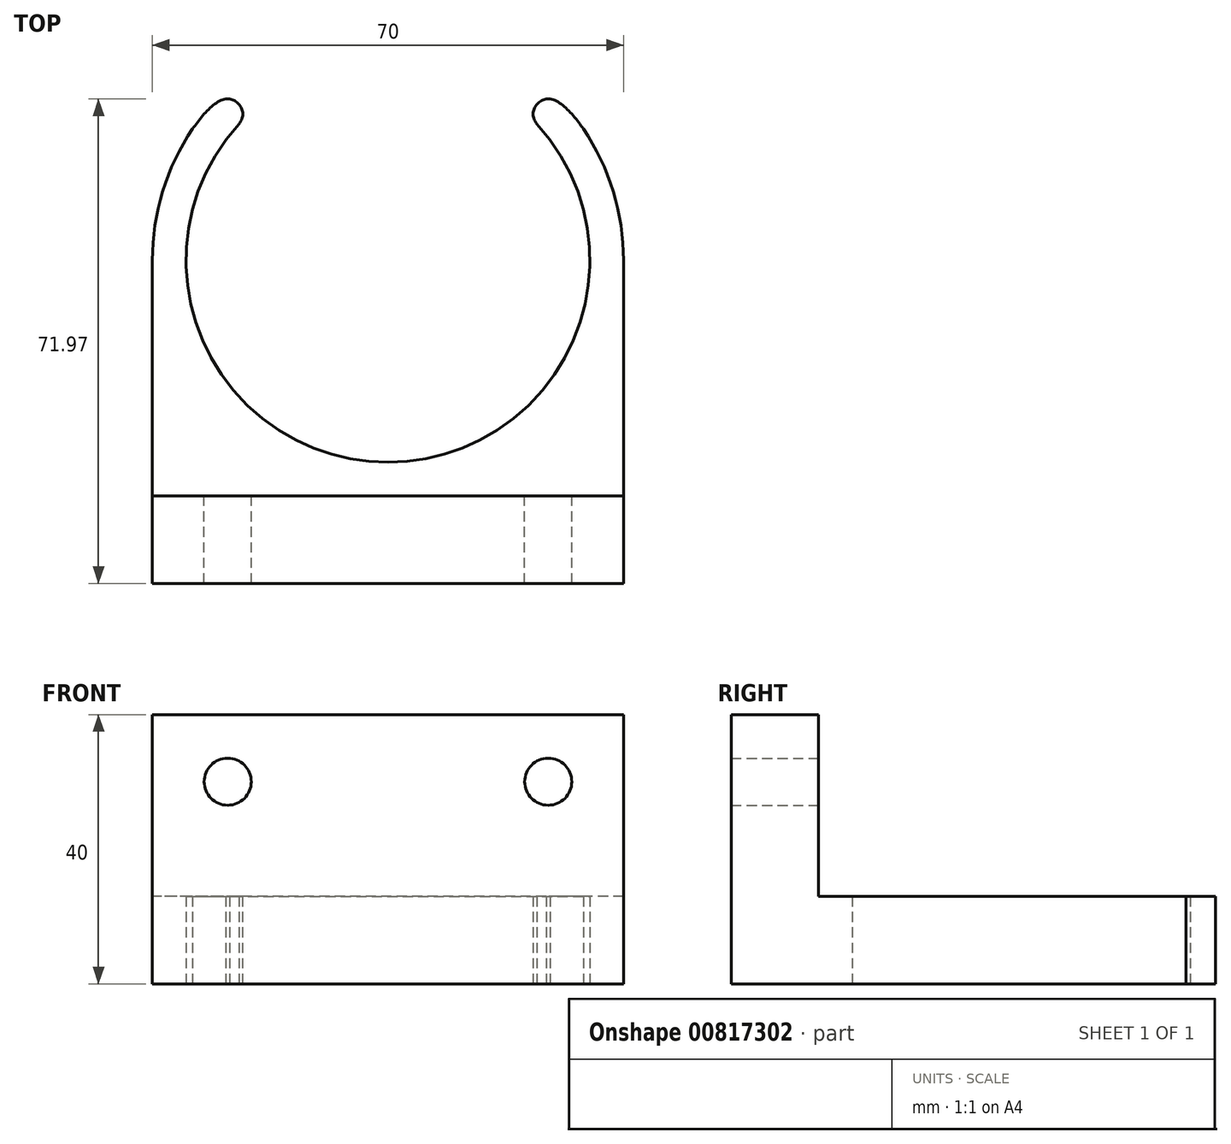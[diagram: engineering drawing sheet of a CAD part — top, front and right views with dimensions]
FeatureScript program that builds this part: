
annotation { "Feature Type Name" : "Feature", "Feature Type Description" : "" }
export const myFeature = defineFeature(function(context is Context, id is Id, definition is map)
    precondition{}
    {
        {
            var Q0;
            Q0=qCreatedBy(makeId("Top.planeOp"),FACE);
            var sketch = newSketch(context, id + "F0", { "sketchPlane" : qUnion([Q0])});
            skArc(sketch, "E0", {"start": v(0, -35) * mm, "mid": v(24.75, 24.75) * mm, "end": v(-35, 0) * mm});
            skLineSegment(sketch, "E1", {"start": v(-25.5, 23.97) * mm, "end": v(25.5, 23.97) * mm});
            skCircle(sketch, "E2.0", {"center": v(0, 0) * mm, "radius": 30 * mm});
            skPoint(sketch, "E3", {"position": v(-35, 0) * mm});
            skPoint(sketch, "E4", {"position": v(35, 0) * mm});
            skPoint(sketch, "E5", {"position": v(0, -35) * mm});
            skLineSegment(sketch, "E6.bottom", {"start": v(-30, 0) * mm, "end": v(35, 0) * mm});
            skLineSegment(sketch, "E6.top", {"start": v(-35, -35) * mm, "end": v(35, -35) * mm});
            skLineSegment(sketch, "E6.left", {"start": v(-35, 0) * mm, "end": v(-35, -35) * mm});
            skLineSegment(sketch, "E6.right", {"start": v(35, 0) * mm, "end": v(35, -35) * mm});
            skLineSegment(sketch, "E7.top", {"start": v(-35, -48) * mm, "end": v(35, -48) * mm});
            skLineSegment(sketch, "E7.left", {"start": v(-35, -35) * mm, "end": v(-35, -48) * mm});
            skLineSegment(sketch, "E7.right", {"start": v(35, -35) * mm, "end": v(35, -48) * mm});
            skLineSegment(sketch, "E8", {"start": v(-25.5, 23.97) * mm, "end": v(-18.03, 23.97) * mm});
            skPoint(sketch, "E9", {"position": v(-23.52, 23.97) * mm});
            skFitSpline(sketch, "E10", {"points": [v(-29.03, 19.55) * mm, v(-23.52, 23.97) * mm, v(-22.3, 20.07) * mm], "startDerivative": vector(7.32, 10.12) * mm, "endDerivative": vector(-11.25, -11.56) * mm});
            skFitSpline(sketch, "E11.MirrorCS", {"points": [v(29.03, 19.55) * mm, v(23.52, 23.97) * mm, v(22.3, 20.07) * mm], "startDerivative": vector(-7.32, 10.12) * mm, "endDerivative": vector(11.25, -11.56) * mm});
            skSolve(sketch);
        }
        {
            var Q0;
            {var subQ0=sQuery(id+"F0.wireOp",EDGE,"E11.MirrorCS");var subQ5=sQuery(id+"F0.wireOp",EDGE,"E1");var subQ6=makeQuery(id+"F0.imprint","INTERSECT",VERTEX,{"disambiguationData":[OD(0.0)],"derivedFrom":[subQ5,subQ0]});Q0=makeQuery(id+"F0.imprint","IMPRINT",FACE,{"disambiguationData":[TD([[makeQuery(id+"F0.imprint","IMPRINT",EDGE,{"disambiguationData":[TD([[subQ6,-1.0]])],"derivedFrom":subQ5}),-1.0]])]});}
            var Q1;
            {var subQ0=sQuery(id+"F0.wireOp",EDGE,"E6.left");Q1=makeQuery(id+"F0.imprint","IMPRINT",FACE,{"disambiguationData":[TD([[makeQuery(id+"F0.imprint","IMPRINT",EDGE,{"derivedFrom":subQ0}),1.0]])]});}
            var Q2;
            {var subQ3=sQuery(id+"F0.wireOp",EDGE,"E6.right");Q2=makeQuery(id+"F0.imprint","IMPRINT",FACE,{"disambiguationData":[TD([[makeQuery(id+"F0.imprint","IMPRINT",EDGE,{"derivedFrom":subQ3}),-1.0]])]});}
            var Q3;
            Q3=makeQuery(id+"F0.imprint","IMPRINT",FACE,{"disambiguationData":[TD([[makeQuery(id+"F0.imprint","IMPRINT",EDGE,{"derivedFrom":sQuery(id+"F0.wireOp",EDGE,"E7.top")}),1.0]])]});
            extrude(context, id + "F1", {"entities" : qUnion([Q0, Q1, Q2, Q3]), "depth" : 13 * mm, "offsetDistance" : 25 * mm});
        }
        {
            var Q0;
            Q0=makeQuery(id+"F0.imprint","IMPRINT",FACE,{"disambiguationData":[TD([[makeQuery(id+"F0.imprint","IMPRINT",EDGE,{"derivedFrom":sQuery(id+"F0.wireOp",EDGE,"E7.top")}),1.0]])]});
            extrude(context, id + "F2", {"entities" : qUnion([Q0]), "operationType" : NewBodyOperationType.ADD, "depth" : 40 * mm, "offsetDistance" : 25 * mm});
        }
        {
            var Q0;
            Q0=qCreatedBy(makeId("Front.planeOp"),FACE);
            var sketch = newSketch(context, id + "F3", { "sketchPlane" : qUnion([Q0])});
            skPoint(sketch, "E12", {"position": v(-23.81, 30.03) * mm});
            skPoint(sketch, "E13.MirrorP", {"position": v(23.81, 30.03) * mm});
            skSolve(sketch);
        }
        {
            var Q0;
            Q0=sQuery(id+"F3.wireOp",VERTEX,"E12");
            var Q1;
            Q1=sQuery(id+"F3.wireOp",VERTEX,"E13.MirrorP");
            var Q2;
            Q2=makeQuery(id+"F1.opExtrude","SWEPT_BODY",BODY,{"disambiguationData":[OSD([sQuery(id+"F0.wireOp",EDGE,"E0"),sQuery(id+"F0.wireOp",EDGE,"E1"),sQuery(id+"F0.wireOp",EDGE,"E2.0"),sQuery(id+"F0.wireOp",EDGE,"E6.left"),sQuery(id+"F0.wireOp",EDGE,"E6.right"),sQuery(id+"F0.wireOp",EDGE,"E7.top"),sQuery(id+"F0.wireOp",EDGE,"E7.left"),sQuery(id+"F0.wireOp",EDGE,"E7.right"),sQuery(id+"F0.wireOp",EDGE,"E8"),sQuery(id+"F0.wireOp",EDGE,"E10"),sQuery(id+"F0.wireOp",EDGE,"E11.MirrorCS")])]});
            hole(context, id + "F4", {"style" : HoleStyle.SIMPLE, "endStyle" : HoleEndStyle.THROUGH, "oppositeDirection" : true, "holeDiameter" : 7 * mm, "majorDiameter" : 5 * mm, "isTappedThrough" : true, "tappedDepth" : 12 * mm, "tapClearance" : 3, "locations" : qUnion([Q0, Q1]), "scope" : qUnion([Q2])});
        }
    });
